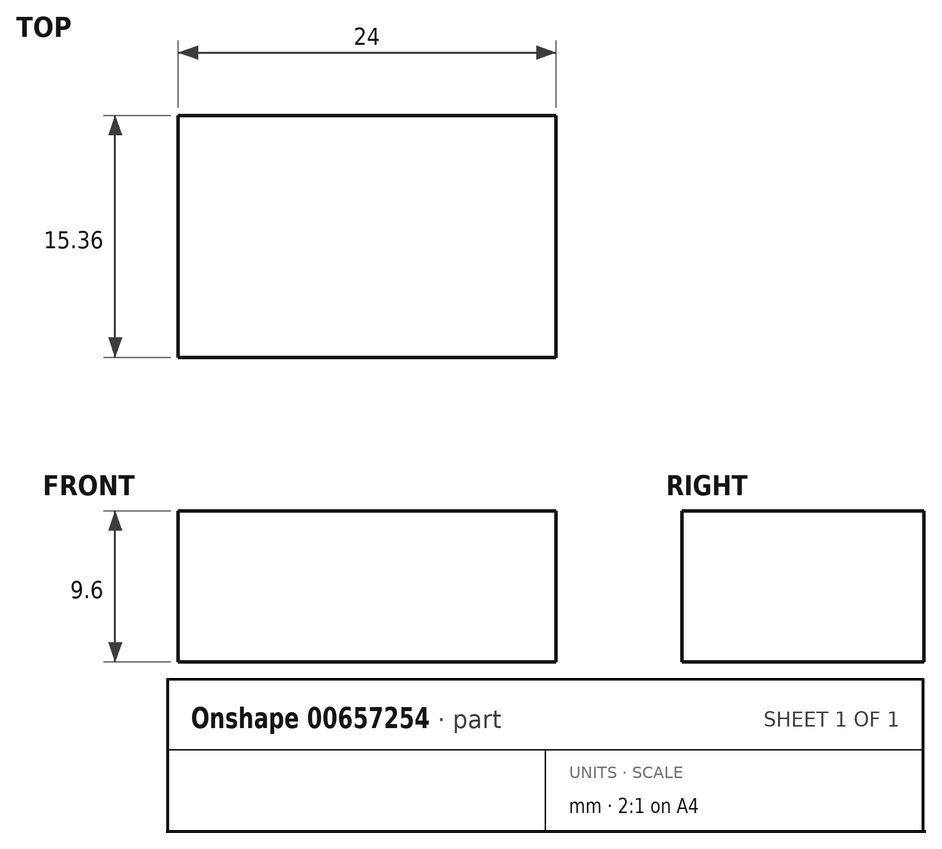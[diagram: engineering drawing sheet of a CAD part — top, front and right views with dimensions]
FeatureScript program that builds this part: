
annotation { "Feature Type Name" : "Feature", "Feature Type Description" : "" }
export const myFeature = defineFeature(function(context is Context, id is Id, definition is map)
    precondition{}
    {
        {
            var Q0;
            Q0=qCreatedBy(makeId("Top.planeOp"),FACE);
            var sketch = newSketch(context, id + "F0", { "sketchPlane" : qUnion([Q0])});
            skLineSegment(sketch, "E0.bottom", {"start": v(0, 0) * mm, "end": v(-24, 0) * mm});
            skLineSegment(sketch, "E0.top", {"start": v(0, 15.36) * mm, "end": v(-24, 15.36) * mm});
            skLineSegment(sketch, "E0.left", {"start": v(0, 0) * mm, "end": v(0, 15.36) * mm});
            skLineSegment(sketch, "E0.right", {"start": v(-24, 0) * mm, "end": v(-24, 15.36) * mm});
            skSolve(sketch);
        }
        {
            var Q0;
            Q0=makeQuery(id+"F0.imprint","IMPRINT",FACE,{"disambiguationData":[TD([[makeQuery(id+"F0.imprint","IMPRINT",EDGE,{"derivedFrom":sQuery(id+"F0.wireOp",EDGE,"E0.bottom")}),-1.0]])]});
            extrude(context, id + "F1", {"entities" : qUnion([Q0]), "depth" : 9.6 * mm, "offsetDistance" : 25.4 * mm});
        }
    });
